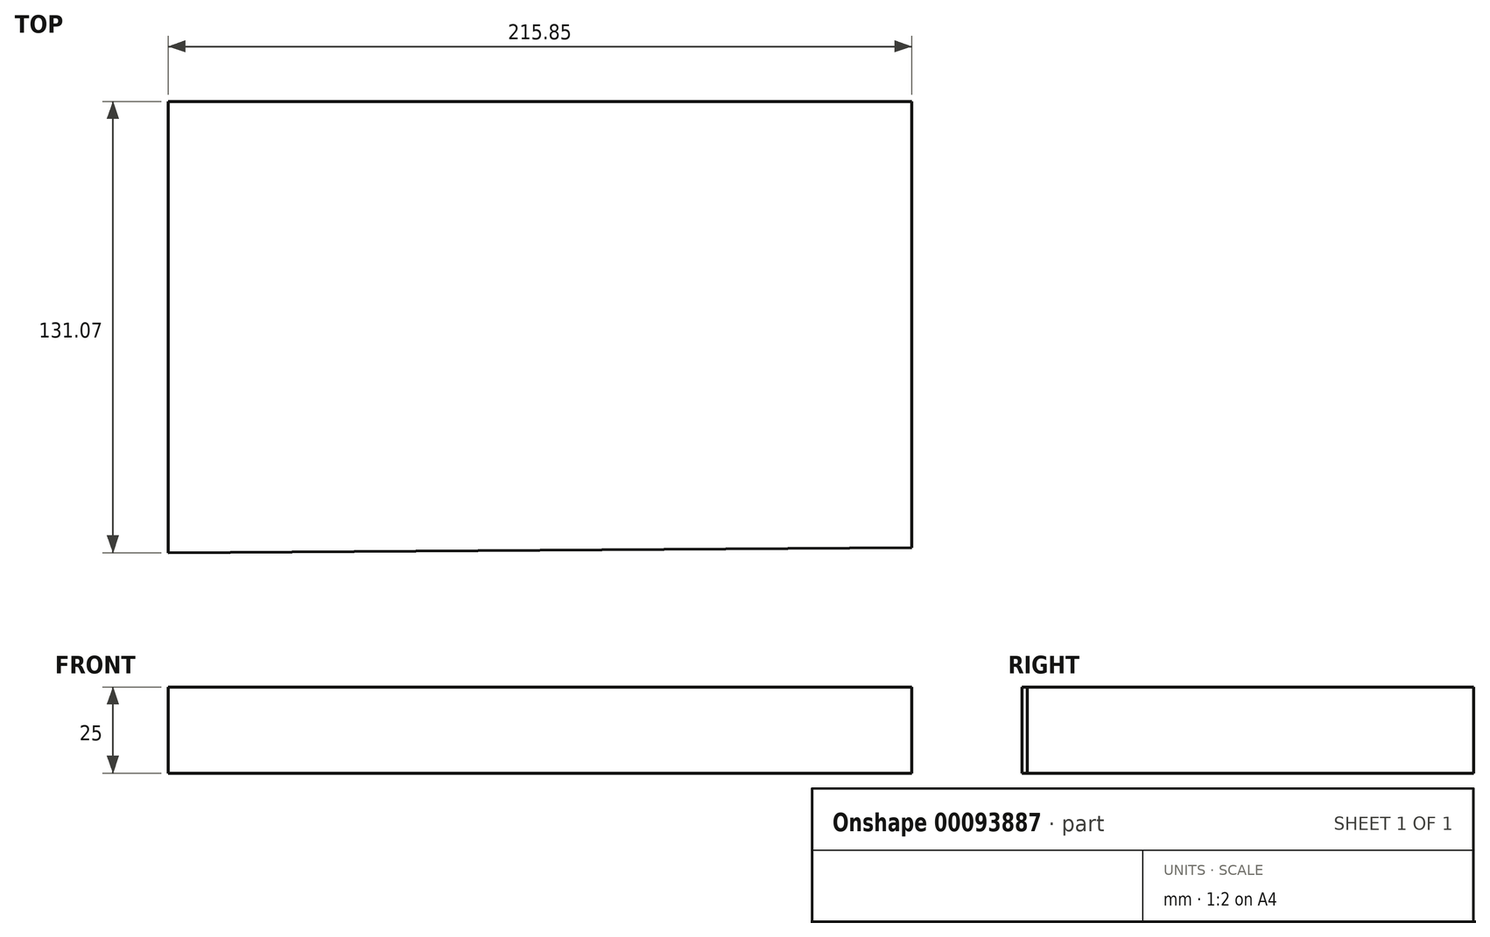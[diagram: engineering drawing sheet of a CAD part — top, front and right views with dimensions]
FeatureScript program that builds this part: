
annotation { "Feature Type Name" : "Feature", "Feature Type Description" : "" }
export const myFeature = defineFeature(function(context is Context, id is Id, definition is map)
    precondition{}
    {
        {
            var Q0;
            Q0=qCreatedBy(makeId("Top.planeOp"),FACE);
            var sketch = newSketch(context, id + "F0", { "sketchPlane" : qUnion([Q0])});
            skLineSegment(sketch, "E0", {"start": v(-122.45, -71.04) * mm, "end": v(-122.45, 60.03) * mm});
            skLineSegment(sketch, "E1", {"start": v(-122.45, 60.03) * mm, "end": v(93.4, 60.03) * mm});
            skLineSegment(sketch, "E2", {"start": v(93.4, 60.03) * mm, "end": v(93.4, -69.57) * mm});
            skLineSegment(sketch, "E3", {"start": v(93.4, -69.57) * mm, "end": v(-122.45, -71.04) * mm});
            skSolve(sketch);
        }
        {
            var Q0;
            Q0=makeQuery(id+"F0.imprint","IMPRINT",FACE,{"disambiguationData":[TD([[makeQuery(id+"F0.imprint","IMPRINT",EDGE,{"derivedFrom":sQuery(id+"F0.wireOp",EDGE,"E0")}),-1.0]])]});
            extrude(context, id + "F1", {"entities" : qUnion([Q0]), "endBound" : BoundingType.SYMMETRIC, "depth" : 25 * mm});
        }
    });
